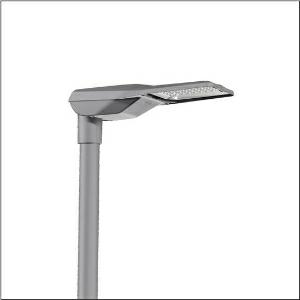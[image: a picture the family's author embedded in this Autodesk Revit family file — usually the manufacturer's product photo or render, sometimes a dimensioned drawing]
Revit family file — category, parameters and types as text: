
# Revit family: streetlight_sl_21_iq_mini___st1_0ab_5xe2m31g08gb_4c82
name_source: partatom
category: Lighting Fixtures
units: mm (PartAtom-declared; Revit-internal decimal feet)

## family parameters
Cut with Voids When Loaded = No
Host = Face
Light Source = No
Part Type = Normal
Room Calculation Point = No
Round Connector Dimension = Use Diameter
Shared = No

## types (1)
- --- (1 x LED, 5000 lm, 37.1 W, 3000K)
    Apparent Load = 37 VA
    CIE Flux Codes = 38 73 97 100 100
    Color Rendering = 70
    Color Temperature = 3000K
    Default Elevation = 1800 mm
    Description = Streetlight SL 21 iQ mini, mast luminaire, primary light control with lens, of PMMA, primary optical cover: cover, of toughened safety glass, transparent, light distribution: ST1.0aB, light emission: direct distribution, primary light characteristic: asymmetric, installation type: post-top, side-entry, LED, High Power LED, rated luminous flux: 5.000lm, luminous efficacy: 135lm/W, light colour: 730, colour temperature: 3000K, control gear: iQ Street-Remote, control: Street-Remote, Auto-Match, Temp-Guard, Lumen-Switch, Night-Set, Smart-Wire, Light-Fading, Desk-Remote (wireless, voltage-free reading and setting of iQ features in the workshop via application-optimized NFC function/RFID function), optimised constant luminous flux control (CLO 2.0), pre-setting: linear dimming characteristic, mains connection: 220..240V, AC, 50/60Hz, start of lifetime: 37W, end of service life: 39W, reduction: 18W, luminaire housing, of diecast aluminium, powder-coated, Siteco® metallic grey (DB 702S), corrosivity category C5 mid according to DIN EN ISO 12944, please order mast flange separately, inclination adjustable: 0°, 5°, 10°, 15°, sealing non-destructively replaceable, multi-level sealing system, length: 628mm, width: 235mm, height: 110mm, mast flange for spigot size: 42mm (side-entry): 5XC10008XM4, 60/48mm (side-entry/post-top): 5XC10108XM2, 76/60mm (side-entry/post-top): 5XC10108XM1, mounting height: 4..8m, protection rating (complete): IP66, insulation class (complete): insulation class II (safety insulation), certification: CE, ENEC, ENEC+, VDE, impact resistance: IK10, permissible operating ambient temperature for outdoor applications: -40..+50°C, standard-compliant lighting for roads and squares, packaging unit: 1 piece

Light Distribution: ST1.0aB
    Height = 110 mm
    Lamp = 1 x LED
    Lamp Light Flux = 5000 lm
    Lamp Power = 37.1 W
    Lamp count = 1
    Length = 625 mm
    Luminous efficacy = 135 lm/W
    Manufacturer = Siteco
    ModVariant = No
    Model = 5XE2M31G08GB
    Number of Poles = 1
    OnlyDefault = Yes
    Power Factor = 1
    Product Name = Streetlight SL 21 iQ mini | ST1.0aB
    Product group = mast luminaire | pylon top
    ProductGroupID = 6100
    Protection Class = Protection class II
    Protection Degree = IP 66
    RLX_Detail_Level = 1
    RLX_Emergency_Light_Flux = 0 lm
    RLX_Emergency_Type = 0
    RLX_Emergency_Type_DB = No
    RlxData = <blob elided: 26313 chars, md5=75e42159>
    Socket = socket
    Standby Power = 0 W
    System Light Flux = 5000 lm
    System Power = 37 W
    Type Comments = factory setting: luminous flux: 100 % | dim-lin: 254 | 385 mA
    Type Image = l_1003519.jpg
    URL = http://relux.com
    VarID = @adj_204029
    Voltage = 0 V
    Weight = 0.00 kg
    Width = 234 mm

## geometry (parser evidence)
native form markers: Blend x4, Sweep x11
no freeform markers — native parametric forms only
